# Revit family: Kessel 93004R en
name_source: partatom
category: Plumbing Fixtures
revit_build: Autodesk Revit Architecture 2014 (Build: 20130308_1515(x64)
units: mm (PartAtom-declared; Revit-internal decimal feet)

## types (1)
- Kessel 93004R en
    <1.010.00.2> Number of the part of the guideline = 98
    <1.010.00.3> Issue date (month) of the guideline = 200601
    <1.010.00.4> Manufacturer name = Kessel
    <1.010.00.5> Revision date of the file = 20190227
    <1.800.00.3> BS number = 001002000001006011010008014001002002007???00700008???
    <1.800.00.4> Comment field = EasyClean modular grease separator, NS 4, Standard, 2-piece
    <1.810.00.3> Manufacturer’s reference number = 93004-R
    <1.810.00.4> DATANORM number = 93004-R
    <1.810.00.6> GTIN number = 4026092071236
    <1.960/3L.00.8> Link (URL) = http://www.kessel.de
    <98.100.00.4> Area of application = Grease separator
    <98.110.00.4> Product series = EasyClean modular grease separator
    <98.200.00.3> Installation of the separators (DIN 19901) = Freestanding
    <98.250.00.3> Disposal variant = Standard
    <98.260.00.3> Sludge trap content (liters) = 400
    <98.300.00.3> Separator content (liters) = 560
    <98.350.00.3> Fat storage (liters) = 160
    <98.360.00.3> Total volume (liters) = 960
    <98.400.00.3> Layer thickness measurement (SonicControl) = no
    <98.450.00.3> Inlet nominal diameter (DN) = 100
    <98.460.00.3> Outlet nominal diameter (DN) = 100
    <98.500.00.3> Nominal size (NS) = 4
    <98.700.00.4> Product name = EasyClean modular grease separator, NS 4, Standard, 2-piece
    CONNECTOR0_DIAMETER_dX_0r = 0 mm  [stored 0 ft]
    CONNECTOR0_dX_00 = 750 mm  [stored 2.46063 ft]
    CONNECTOR0_dX_01 = 578 mm
    CONNECTOR0_ref_dX = 578 mm
    CONNECTOR0_ref_dZ = 1205 mm
    CONNECTOR1_DIAMETER_dX_0r = 0 mm  [stored 0 ft]
    CONNECTOR1_dX_00 = 602 mm
    CONNECTOR1_dX_01 = 750 mm  [stored 2.46063 ft]
    CONNECTOR1_ref_dX = 602 mm
    CONNECTOR1_ref_dZ = 1135 mm
    Manufacturer = Kessel
    Model = 93004-R
    URL = www.kessel.com

note: [stored X ft] marks values corroborated as IEEE doubles in the binary element streams (Revit-internal decimal feet)
